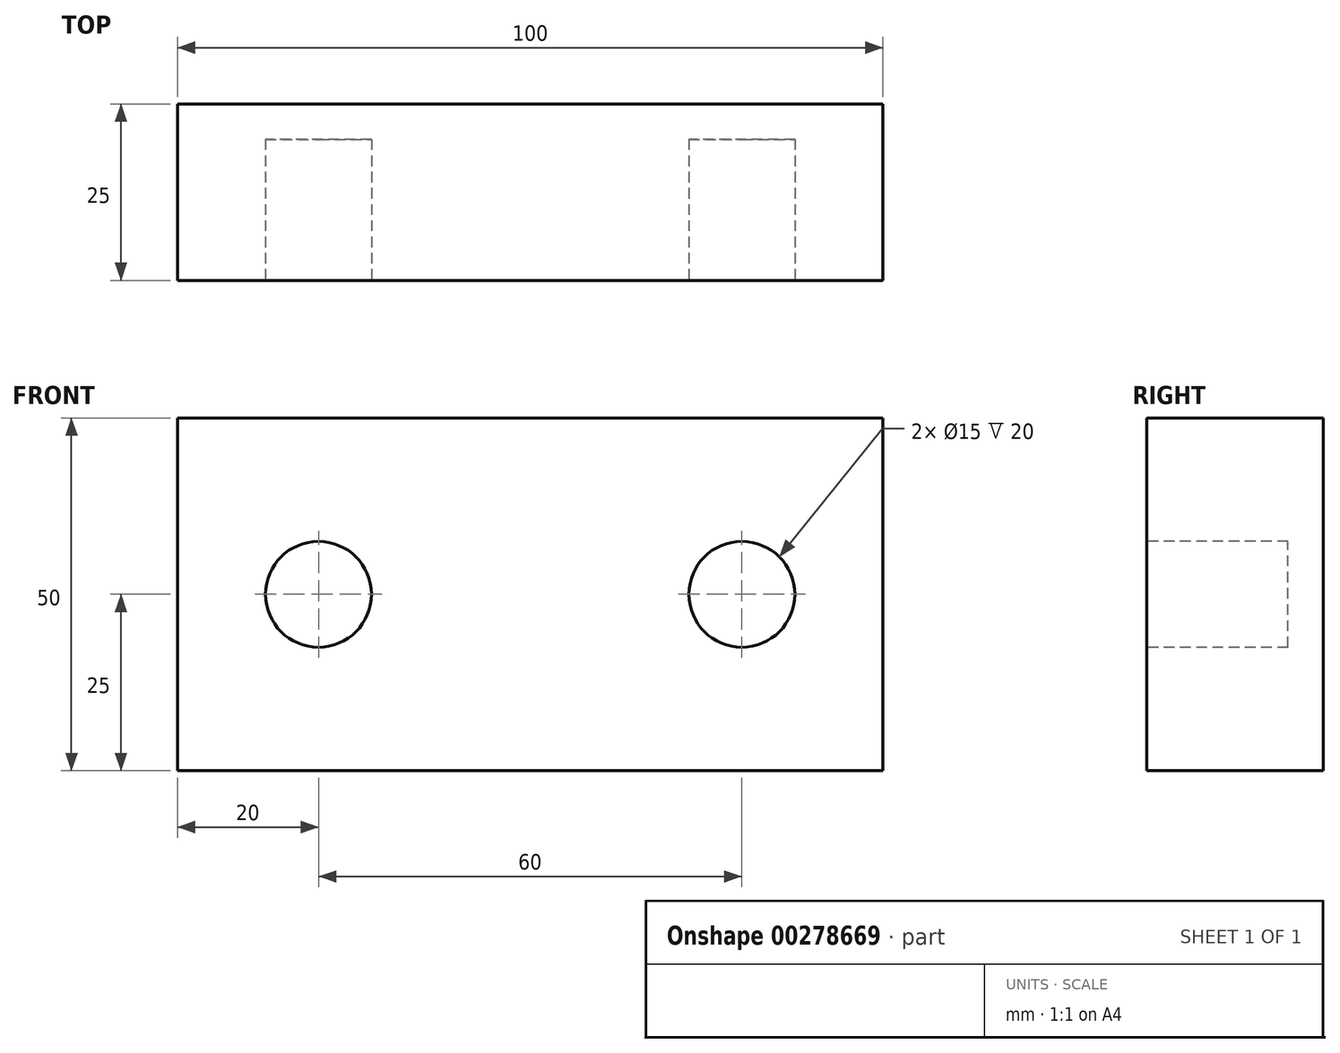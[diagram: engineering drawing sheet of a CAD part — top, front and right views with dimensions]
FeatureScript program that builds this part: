
annotation { "Feature Type Name" : "Feature", "Feature Type Description" : "" }
export const myFeature = defineFeature(function(context is Context, id is Id, definition is map)
    precondition{}
    {
        {
            var Q0;
            Q0=qCreatedBy(makeId("Front.planeOp"),FACE);
            var sketch = newSketch(context, id + "F0", { "sketchPlane" : qUnion([Q0])});
            skLineSegment(sketch, "E0.bottom", {"start": v(-50, 25) * mm, "end": v(50, 25) * mm});
            skLineSegment(sketch, "E0.top", {"start": v(-50, -25) * mm, "end": v(50, -25) * mm});
            skLineSegment(sketch, "E0.left", {"start": v(-50, 25) * mm, "end": v(-50, -25) * mm});
            skLineSegment(sketch, "E0.right", {"start": v(50, 25) * mm, "end": v(50, -25) * mm});
            skSolve(sketch);
        }
        {
            var Q0;
            Q0 = qSketchRegion(id + "F0", true);
            extrude(context, id + "F1", {"entities" : qUnion([Q0]), "depth" : 25 * mm, "offsetDistance" : 25 * mm});
        }
        {
            var Q0;
            Q0=makeQuery(id+"F1.opExtrude","CAP_FACE",FACE,{"disambiguationData":[OSD([sQuery(id+"F0.wireOp",EDGE,"E0.bottom"),sQuery(id+"F0.wireOp",EDGE,"E0.top"),sQuery(id+"F0.wireOp",EDGE,"E0.left"),sQuery(id+"F0.wireOp",EDGE,"E0.right")])],"isStart":false});
            var sketch = newSketch(context, id + "F2", { "sketchPlane" : qUnion([Q0])});
            skCircle(sketch, "E1", {"center": v(-30, 0) * mm, "radius": 7.5 * mm});
            skCircle(sketch, "E2", {"center": v(30, 0) * mm, "radius": 7.5 * mm});
            skSolve(sketch);
        }
        {
            var Q0;
            Q0 = qSketchRegion(id + "F2", true);
            extrude(context, id + "F3", {"entities" : qUnion([Q0]), "operationType" : NewBodyOperationType.REMOVE, "oppositeDirection" : true, "depth" : 20 * mm, "offsetDistance" : 25 * mm});
        }
    });
